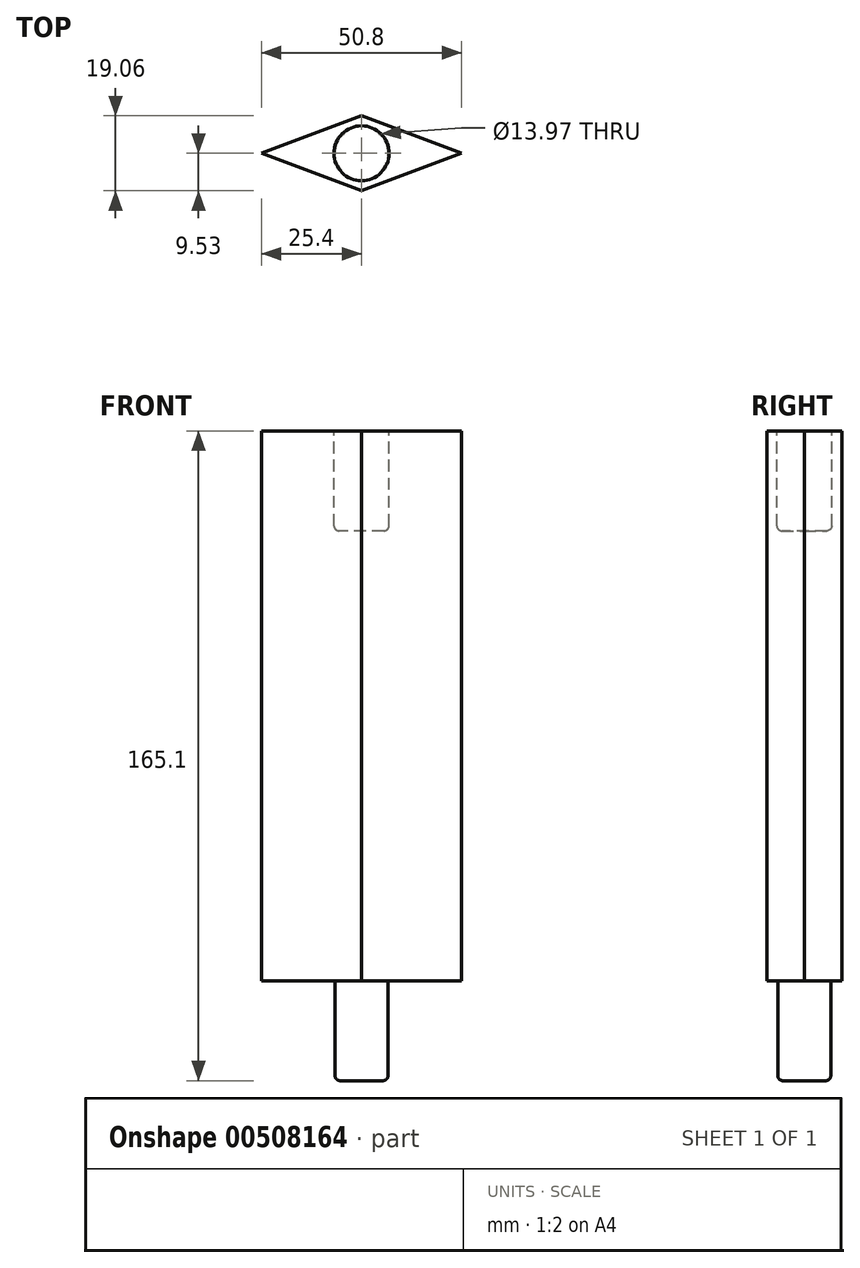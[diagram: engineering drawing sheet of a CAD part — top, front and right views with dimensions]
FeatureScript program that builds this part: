
annotation { "Feature Type Name" : "Feature", "Feature Type Description" : "" }
export const myFeature = defineFeature(function(context is Context, id is Id, definition is map)
    precondition{}
    {
        {
            var Q0;
            Q0=qCreatedBy(makeId("Top.planeOp"),FACE);
            var sketch = newSketch(context, id + "F0", { "sketchPlane" : qUnion([Q0])});
            skLineSegment(sketch, "E0", {"start": v(0, 0) * mm, "end": v(0, 9.53) * mm, "construction": true});
            skLineSegment(sketch, "E1", {"start": v(0, 9.53) * mm, "end": v(0, -9.52) * mm, "construction": true});
            skLineSegment(sketch, "E2", {"start": v(-25.4, 0) * mm, "end": v(25.4, 0) * mm, "construction": true});
            skLineSegment(sketch, "E3", {"start": v(0, 9.53) * mm, "end": v(-25.4, 0) * mm});
            skLineSegment(sketch, "E4", {"start": v(0, 9.53) * mm, "end": v(25.4, 0) * mm});
            skLineSegment(sketch, "E5", {"start": v(25.4, 0) * mm, "end": v(0, -9.52) * mm});
            skLineSegment(sketch, "E6", {"start": v(-25.4, 0) * mm, "end": v(0, -9.52) * mm});
            skSolve(sketch);
        }
        {
            var Q0;
            Q0=qSketchRegion(id+"F0",true);
            extrude(context, id + "F1", {"entities" : qUnion([Q0]), "depth" : 139.7 * mm});
        }
        {
            var Q0;
            Q0=qCreatedBy(makeId("Top.planeOp"),FACE);
            var sketch = newSketch(context, id + "F2", { "sketchPlane" : qUnion([Q0])});
            skCircle(sketch, "E7", {"center": v(0, 0) * mm, "radius": 6.73 * mm});
            skSolve(sketch);
        }
        {
            var Q0;
            Q0=qSketchRegion(id+"F2",true);
            extrude(context, id + "F3", {"entities" : qUnion([Q0]), "operationType" : NewBodyOperationType.ADD, "oppositeDirection" : true, "depth" : 25.4 * mm});
        }
        {
            var Q0;
            Q0=makeQuery(id+"F1.opExtrude","CAP_FACE",FACE,{"disambiguationData":[OSD([sQuery(id+"F0.wireOp",EDGE,"E3"),sQuery(id+"F0.wireOp",EDGE,"E4"),sQuery(id+"F0.wireOp",EDGE,"E5"),sQuery(id+"F0.wireOp",EDGE,"E6")])],"isStart":false});
            var sketch = newSketch(context, id + "F4", { "sketchPlane" : qUnion([Q0])});
            skCircle(sketch, "E8", {"center": v(0, 0) * mm, "radius": 6.99 * mm});
            skSolve(sketch);
        }
        {
            var Q0;
            Q0=makeQuery(id+"F4.imprint","IMPRINT",FACE,{"disambiguationData":[TD([[makeQuery(id+"F4.imprint","IMPRINT",EDGE,{"derivedFrom":sQuery(id+"F4.wireOp",EDGE,"E8")}),1.0]])]});
            var Q1;
            Q1=sQuery(id+"F4.wireOp",EDGE,"E8");
            extrude(context, id + "F5", {"entities" : qUnion([Q0]), "operationType" : NewBodyOperationType.REMOVE, "surfaceEntities" : qUnion([Q1]), "oppositeDirection" : true, "depth" : 25.4 * mm});
        }
        {
            var Q0;
            Q0=makeQuery(id+"F5.boolean.opBoolean","COPY",EDGE,{"derivedFrom":makeQuery(id+"F5.opExtrude","CAP_EDGE",EDGE,{"disambiguationData":[OSD([sQuery(id+"F4.wireOp",EDGE,"E8")])],"isStart":false})});
            var Q1;
            Q1=makeQuery(id+"F5.boolean.opBoolean","COPY",EDGE,{"derivedFrom":makeQuery(id+"F5.opExtrude","CAP_EDGE",EDGE,{"disambiguationData":[OSD([sQuery(id+"F4.wireOp",EDGE,"E8")])],"isStart":true})});
            fillet(context, id + "F6", {"entities" : qUnion([Q0, Q1]), "radius" : 1.27 * mm, "tangentPropagation" : true, "allowEdgeOverflow" : false});
        }
        {
            var Q0;
            Q0=makeQuery(id+"F3.opExtrude","CAP_EDGE",EDGE,{"disambiguationData":[OSD([sQuery(id+"F2.wireOp",EDGE,"E7")])],"isStart":false});
            var Q1;
            Q1=makeQuery(id+"F3.opExtrude","CAP_EDGE",EDGE,{"disambiguationData":[OSD([sQuery(id+"F2.wireOp",EDGE,"E7")])],"isStart":true});
            fillet(context, id + "F7", {"entities" : qUnion([Q0, Q1]), "radius" : 1.27 * mm, "tangentPropagation" : true, "allowEdgeOverflow" : false});
        }
    });
